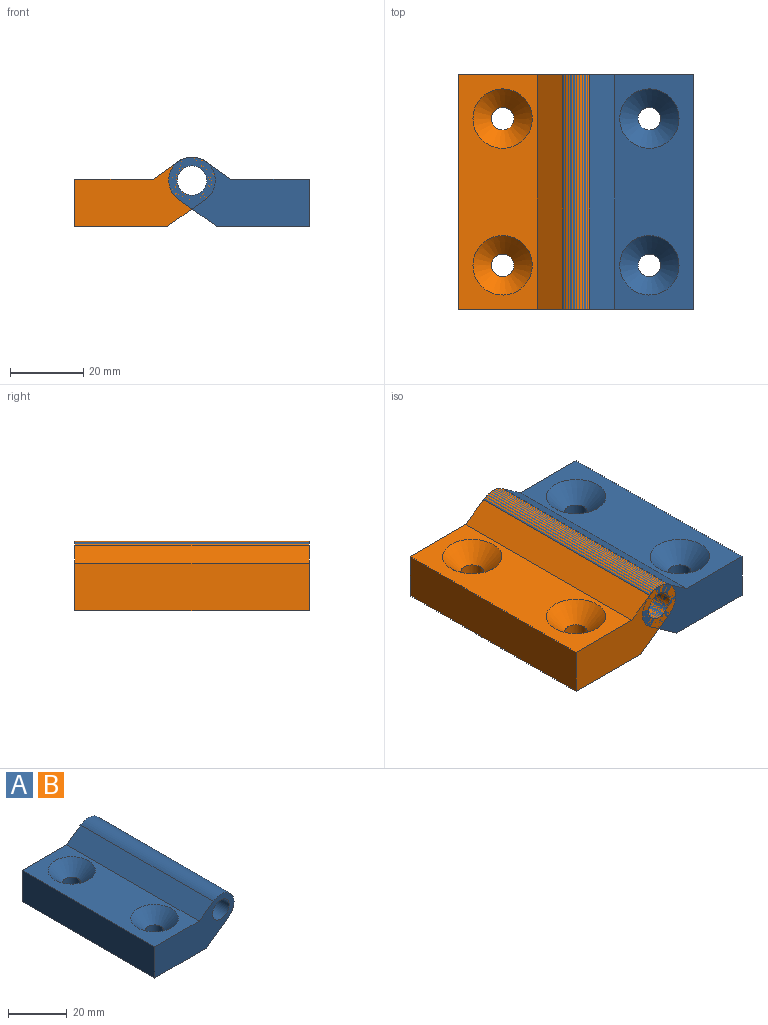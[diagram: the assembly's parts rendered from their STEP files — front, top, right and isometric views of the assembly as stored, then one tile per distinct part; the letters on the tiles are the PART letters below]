
ASSEMBLY  parts=2 mates=1
PART A: 13 faces, bbox 38.4x64x19 mm
  f0: plane 64x10.56mm, normal (0.58,0,-0.82), area 827.8mm2, adj f1,f6,f7,f8
  f1: cylinder r=6.35mm len=64mm, axis (0,1,0), area 1276.7mm2, adj f0,f2,f7,f8
  f2: plane 64x6.85mm, normal (-0.58,0,0.82), area 536.4mm2, adj f1,f3,f7,f8
  f3: plane 64x21.49mm, normal (0,0,1), area 963.2mm2, adj f2,f4,f7,f8,f11,f12
  f4: plane 64x13mm, normal (-1,0,0), area 832mm2, adj f3,f6,f7,f8
  f5: cylinder r=4mm len=64mm, axis (0,1,0), area 1608.5mm2, adj f7,f8
  f6: plane 64x25.1mm, normal (0,0,-1), area 1546mm2, adj f0,f4,f7,f8,f9,f10
  f7: plane 38.35x19mm, normal (0,-1,0), area 451.3mm2, adj f0,f1,f2,f3,f4,f5,f6
  f8: plane 38.35x19mm, normal (0,1,0), area 451.3mm2, adj f0,f1,f2,f3,f4,f5,f6
  f9: cylinder r=3.1mm len=8mm, axis (0,0,1), area 155.8mm2, adj f6,f12
  f10: cylinder r=3.1mm len=8mm, axis (0,0,1), area 155.8mm2, adj f6,f11
  f11: cone r=3.1mm half-angle=45deg, axis (0,0,1), area 248.8mm2, adj f3,f10
  f12: cone r=3.1mm half-angle=45deg, axis (0,0,1), area 248.8mm2, adj f3,f9
PART B: same geometry as A
PLACE A rot(axis=(0,0,-1),180deg) t=(4.82,-39.21,-13.38)mm
PLACE B t=(4.82,24.79,-13.38)mm
MATE revolute A.f1 <-> B.f1  axis (0,1,0) through (4.82,24.79,-0.73)mm
